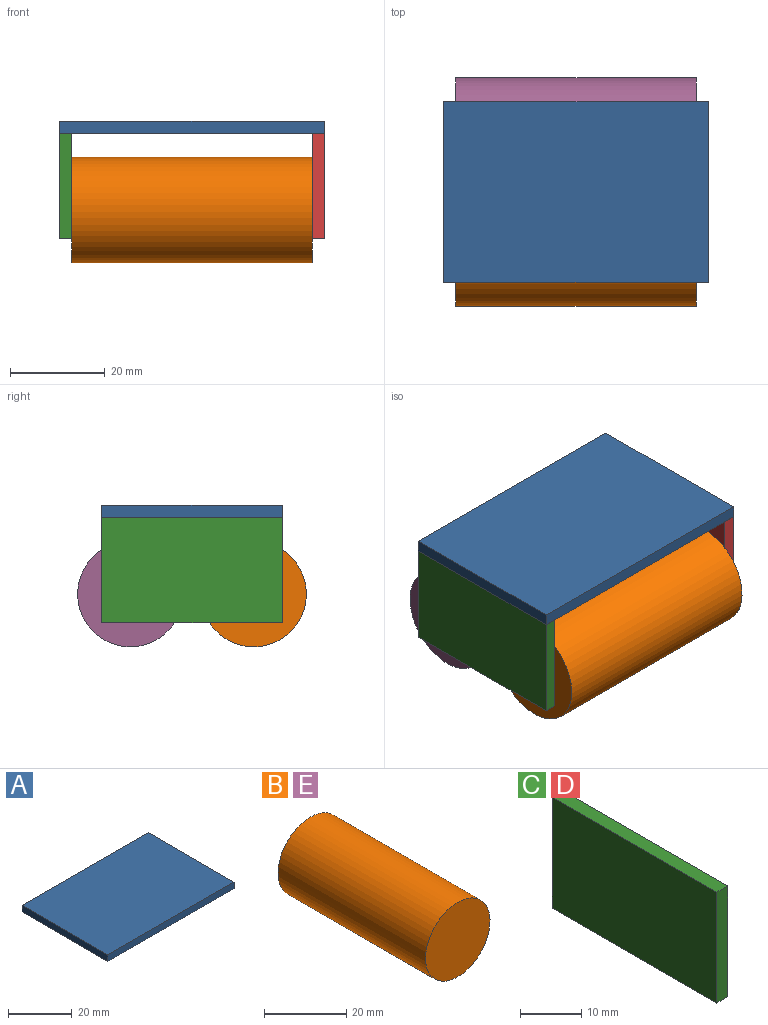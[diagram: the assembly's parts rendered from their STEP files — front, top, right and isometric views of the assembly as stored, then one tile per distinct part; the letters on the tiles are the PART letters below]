
ASSEMBLY  parts=5 mates=4
PART A: 6 faces, bbox 55.9x38.1x2.5 mm
  f0: plane 38.1x2.54mm, normal (-1,0,0), area 96.8mm2, adj f1,f3,f4,f5
  f1: plane 55.88x2.54mm, normal (0,-1,0), area 141.9mm2, adj f0,f2,f4,f5
  f2: plane 38.1x2.54mm, normal (1,0,0), area 96.8mm2, adj f1,f3,f4,f5
  f3: plane 55.88x2.54mm, normal (0,1,0), area 141.9mm2, adj f0,f2,f4,f5
  f4: plane 55.88x38.1mm, normal (0,0,1), area 2129mm2, adj f0,f1,f2,f3
  f5: plane 55.88x38.1mm, normal (0,0,-1), area 2129mm2, adj f0,f1,f2,f3
PART B: 3 faces, bbox 22.2x50.8x22.2 mm
  f0: cylinder r=11.11mm len=50.8mm, axis (0,1,0), area 3547mm2, adj f1,f2
  f1: plane 22.23x22.23mm, normal (0,-1,0), area 387.9mm2, adj f0
  f2: plane 22.23x22.23mm, normal (0,1,0), area 387.9mm2, adj f0
PART C: 6 faces, bbox 2.5x38.1x22.2 mm
  f0: plane 22.23x2.54mm, normal (0,-1,0), area 56.5mm2, adj f1,f3,f4,f5
  f1: plane 38.1x2.54mm, normal (0,0,-1), area 96.8mm2, adj f0,f2,f4,f5
  f2: plane 22.23x2.54mm, normal (0,1,0), area 56.5mm2, adj f1,f3,f4,f5
  f3: plane 38.1x2.54mm, normal (0,0,1), area 96.8mm2, adj f0,f2,f4,f5
  f4: plane 38.1x22.23mm, normal (1,0,0), area 846.8mm2, adj f0,f1,f2,f3
  f5: plane 38.1x22.23mm, normal (-1,0,0), area 846.8mm2, adj f0,f1,f2,f3
PART D: same geometry as C
PART E: same geometry as B
PLACE A t=(-14.34,-22.27,-2.38)mm
PLACE B rot(axis=(0.71,-0.71,0),180deg) t=(-11.8,-16.24,-18.58)mm
PLACE C t=(-14.34,-22.27,-24.61)mm
PLACE D rot(axis=(0,0,-1),180deg) t=(41.54,15.83,-24.61)mm
PLACE E rot(axis=(0.71,-0.71,0),180deg) t=(-11.8,9.79,-18.58)mm
MATE fastened B.f0 <-> C.f4  axis (-1,0,0) through (-11.8,-16.24,-18.58)mm
MATE fastened A.f5 <-> D.f3  axis (0,0,-1) through (41.54,-22.27,-2.38)mm
MATE fastened B.f0 <-> D.f4  axis (1,0,0) through (39,-16.24,-18.58)mm
MATE fastened E.f0 <-> D.f4  axis (1,0,0) through (39,9.79,-18.58)mm
